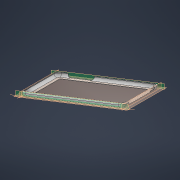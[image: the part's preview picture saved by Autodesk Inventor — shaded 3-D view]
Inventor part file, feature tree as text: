
AUTODESK INVENTOR PART (.ipt)
format: ipt  version: 2021 (Build 250183000, 183)  size: 253,952 bytes
history: native  units: mm
features: extrude x4, sketch x4, fillet x3, plane x2, thicken_offset x1
ambient origin geometry x8: Origin, YZ Plane, XZ Plane, XY Plane, X Axis, Y Axis, Z Axis, Center Point
bodies: Solid1 (feature_tree), Solid2 (feature_tree)
feature tree (14):
  extrude  "Extrusion1"  Depth=5.9mm
  fillet  "Fillet1"  [1 undecoded]
  fillet  "Fillet2"  Radius=9.9mm
  fillet  "Fillet3"  Radius=5.9mm
  thicken_offset  "Thicken1"
  extrude  "Extrusion2"  Depth=8.0mm
  plane  "Work Plane1"
  extrude  "Extrusion3"  Depth=8.0mm
  plane  "Work Plane2"
  extrude  "Extrusion5"  Depth=5.9mm
  sketch  "Sketch1"  dims[d0=208.4mm d1=137.5mm d3=0.0mm d4=9.9mm d6=5.9mm]
  sketch  "Sketch3"  dims[d7=0.8mm d8=0.8mm d14=8.0mm]
  sketch  "Sketch4"  dims[d15=8.0mm d17=8.0mm]
  sketch  "Sketch5"  dims[d18=0.0mm d19=0.0mm d20=53.5mm d21=24.5mm d22=10.0mm d23=0.0mm d24=19.0mm d25=19.0mm d28=5.9mm d29=10.0mm d30=0.0mm d31=5.9mm]
note: 1 required parameter value undecoded (feature->parameter linkage not recoverable at this tier; creation-order binding heuristic only, values carry confidence <= 0.55)
